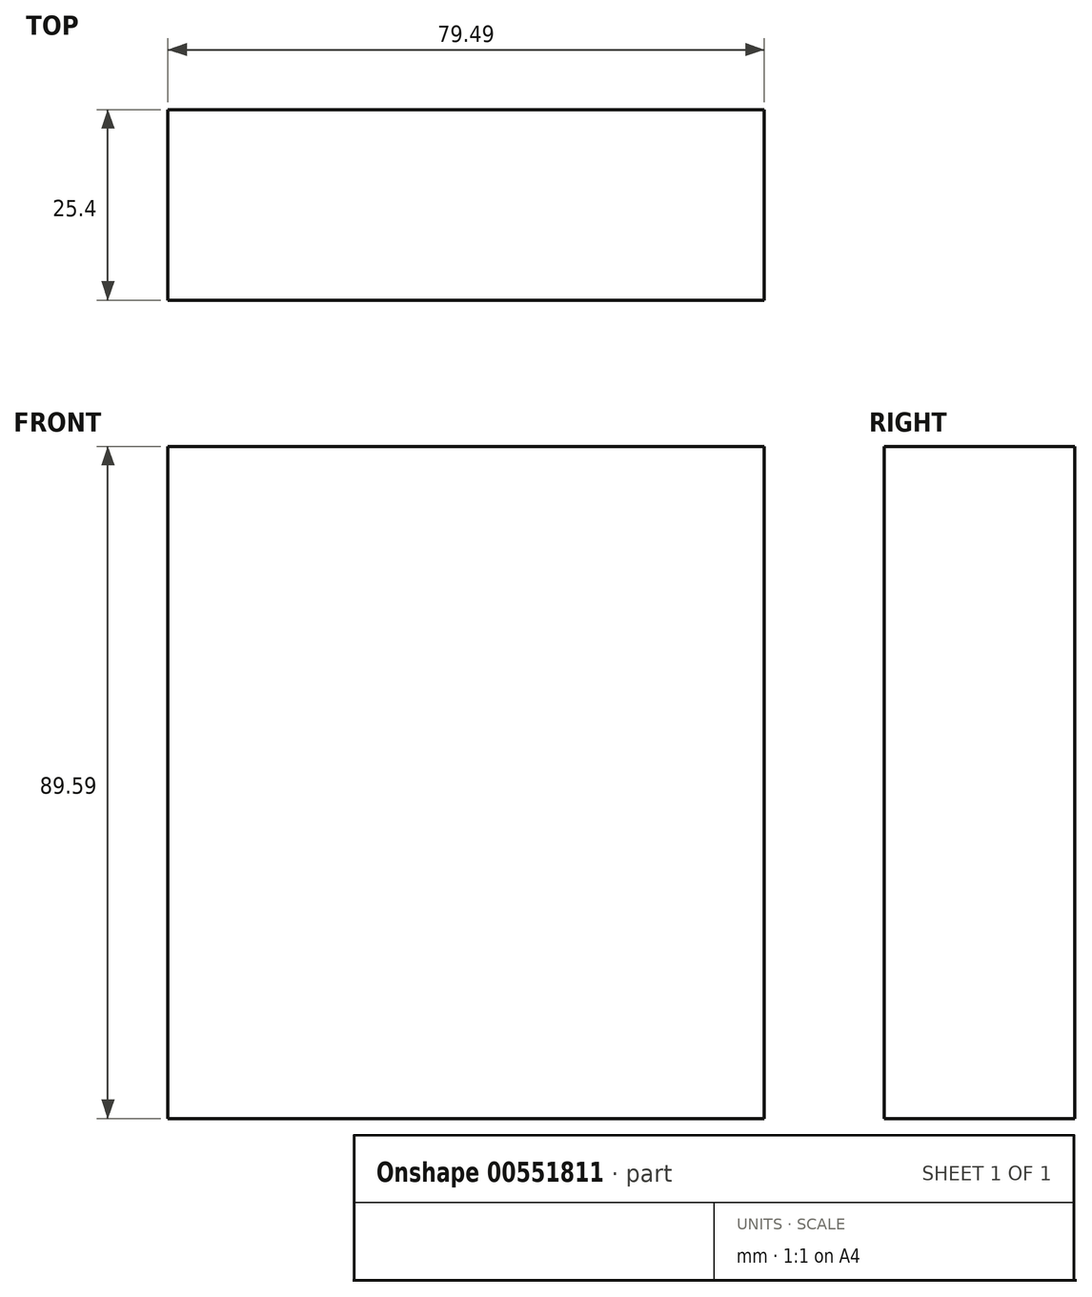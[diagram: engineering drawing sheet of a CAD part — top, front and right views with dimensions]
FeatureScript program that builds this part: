
annotation { "Feature Type Name" : "Feature", "Feature Type Description" : "" }
export const myFeature = defineFeature(function(context is Context, id is Id, definition is map)
    precondition{}
    {
        {
            var Q0;
            Q0=qCreatedBy(makeId("Front.planeOp"),FACE);
            var sketch = newSketch(context, id + "F0", { "sketchPlane" : qUnion([Q0])});
            skLineSegment(sketch, "E0.bottom", {"start": v(-23.27, 45) * mm, "end": v(56.22, 45) * mm});
            skLineSegment(sketch, "E0.top", {"start": v(-23.27, -44.59) * mm, "end": v(56.22, -44.59) * mm});
            skLineSegment(sketch, "E0.left", {"start": v(-23.27, 45) * mm, "end": v(-23.27, -44.59) * mm});
            skLineSegment(sketch, "E0.right", {"start": v(56.22, 45) * mm, "end": v(56.22, -44.59) * mm});
            skSolve(sketch);
        }
        {
            var Q0;
            Q0 = qSketchRegion(id + "F0", true);
            extrude(context, id + "F1", {"entities" : qUnion([Q0]), "depth" : 25.4 * mm, "offsetDistance" : 25.4 * mm});
        }
    });
